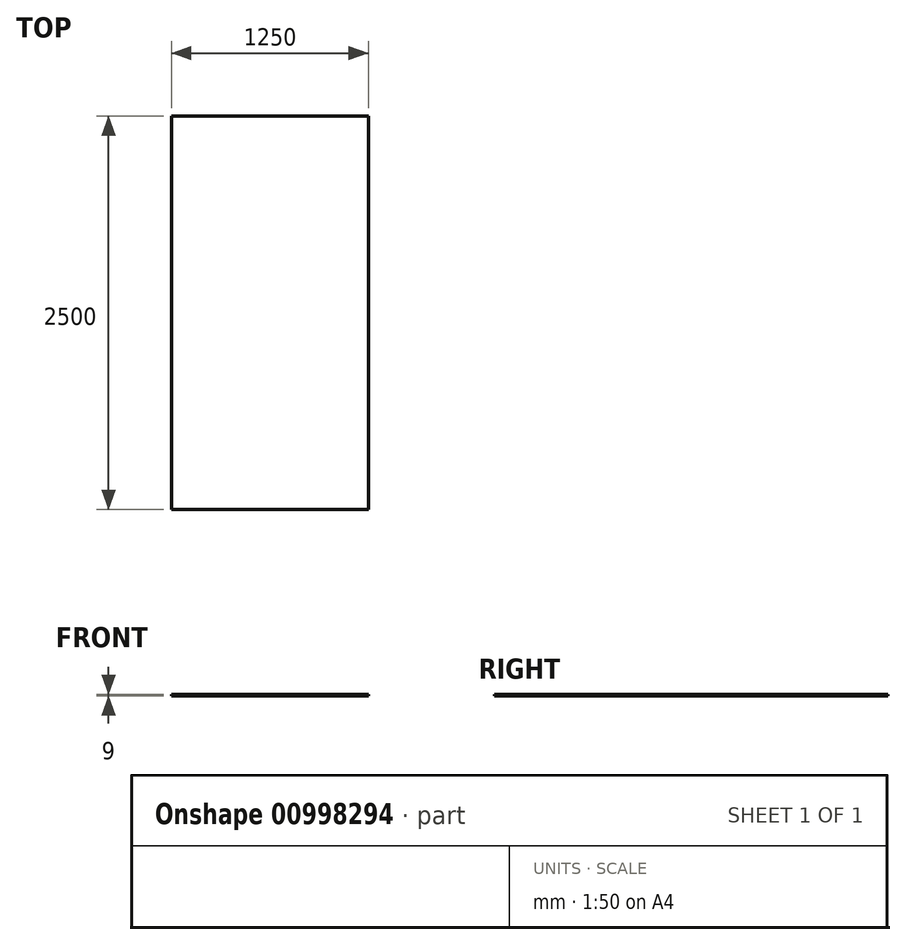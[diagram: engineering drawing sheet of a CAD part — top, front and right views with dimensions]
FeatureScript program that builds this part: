
annotation { "Feature Type Name" : "Feature", "Feature Type Description" : "" }
export const myFeature = defineFeature(function(context is Context, id is Id, definition is map)
    precondition{}
    {
        {
            var Q0;
            Q0=qCreatedBy(makeId("Top.planeOp"),FACE);
            var sketch = newSketch(context, id + "F0", { "sketchPlane" : qUnion([Q0])});
            skLineSegment(sketch, "E0.bottom", {"start": v(625, -1250) * mm, "end": v(-625, -1250) * mm});
            skLineSegment(sketch, "E0.top", {"start": v(625, 1250) * mm, "end": v(-625, 1250) * mm});
            skLineSegment(sketch, "E0.left", {"start": v(625, -1250) * mm, "end": v(625, 1250) * mm});
            skLineSegment(sketch, "E0.right", {"start": v(-625, -1250) * mm, "end": v(-625, 1250) * mm});
            skPoint(sketch, "E0.middle", {"position": v(0, 0) * mm});
            skSolve(sketch);
        }
        {
            var Q0;
            Q0=makeQuery(id+"F0.imprint","IMPRINT",FACE,{"disambiguationData":[TD([[makeQuery(id+"F0.imprint","IMPRINT",EDGE,{"derivedFrom":sQuery(id+"F0.wireOp",EDGE,"E0.bottom")}),-1.0]])]});
            extrude(context, id + "F1", {"entities" : qUnion([Q0]), "depth" : 9 * mm, "offsetDistance" : 25 * mm});
        }
    });
